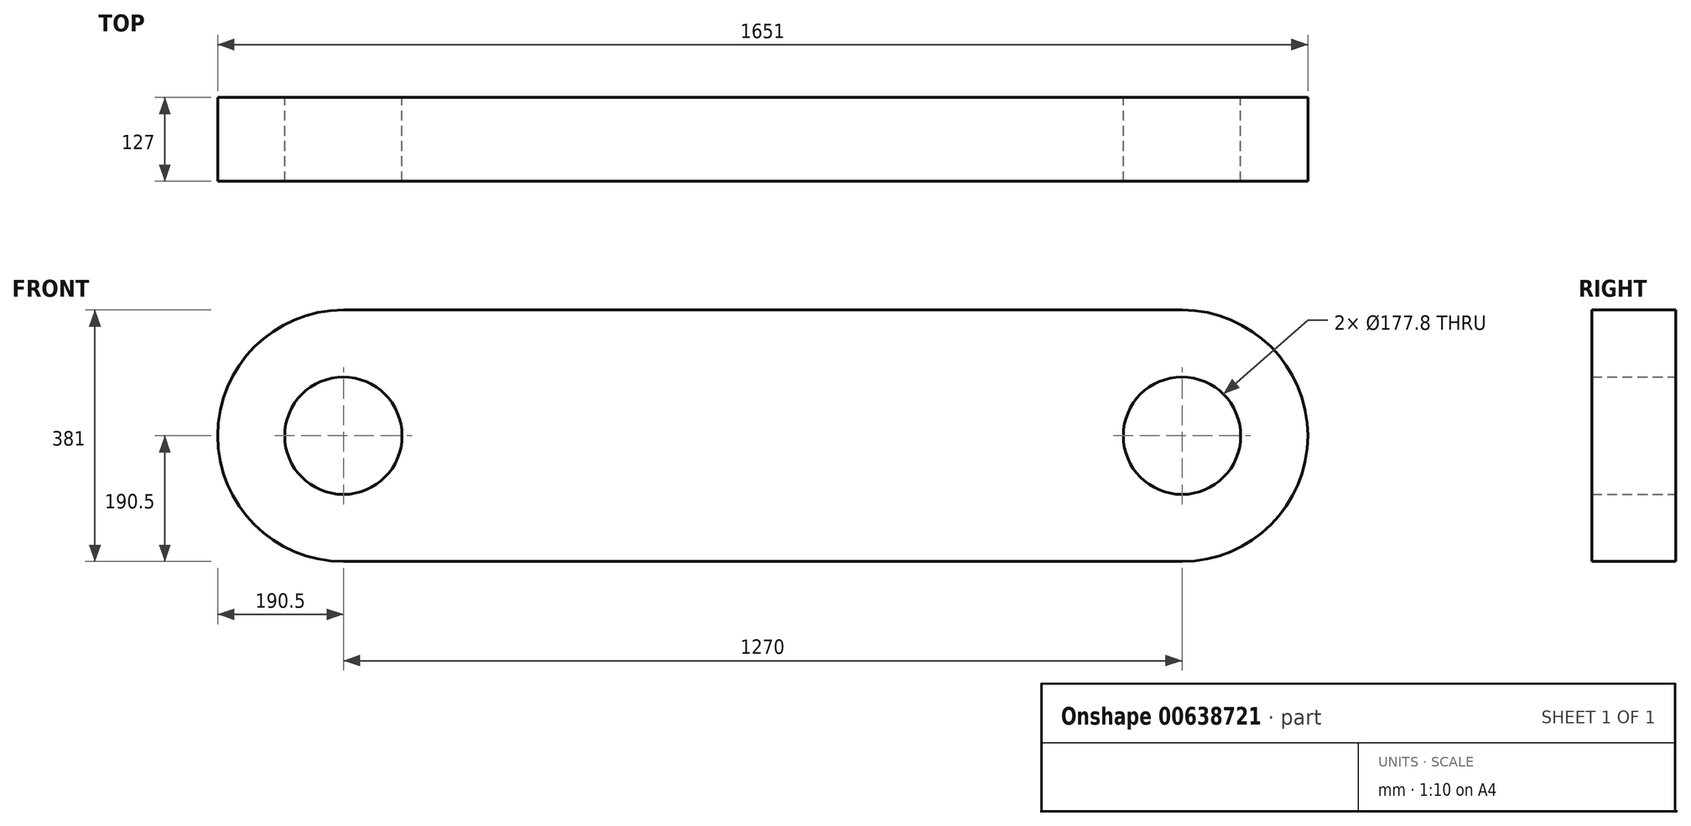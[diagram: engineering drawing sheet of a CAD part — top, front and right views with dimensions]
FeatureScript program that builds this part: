
annotation { "Feature Type Name" : "Feature", "Feature Type Description" : "" }
export const myFeature = defineFeature(function(context is Context, id is Id, definition is map)
    precondition{}
    {
        {
            var Q0;
            Q0=qCreatedBy(makeId("Front.planeOp"),FACE);
            var sketch = newSketch(context, id + "F0", { "sketchPlane" : qUnion([Q0])});
            skArc(sketch, "E0", {"start": v(-635, 190.5) * mm, "mid": v(-825.5, 0) * mm, "end": v(-635, -190.5) * mm});
            skCircle(sketch, "E1", {"center": v(-635, 0) * mm, "radius": 88.9 * mm});
            skLineSegment(sketch, "E2", {"start": v(-635, 190.5) * mm, "end": v(0, 190.5) * mm});
            skLineSegment(sketch, "E3", {"start": v(-635, -190.5) * mm, "end": v(0, -190.5) * mm});
            skArc(sketch, "E4.MirrorCS", {"start": v(635, 190.5) * mm, "mid": v(825.5, 0) * mm, "end": v(635, -190.5) * mm});
            skLineSegment(sketch, "E5.MirrorCS", {"start": v(635, 190.5) * mm, "end": v(0, 190.5) * mm});
            skLineSegment(sketch, "E6.MirrorCS", {"start": v(635, -190.5) * mm, "end": v(0, -190.5) * mm});
            skCircle(sketch, "E7.MirrorC", {"center": v(635, 0) * mm, "radius": 88.9 * mm});
            skSolve(sketch);
        }
        {
            var Q0;
            Q0=makeQuery(id+"F0.imprint","IMPRINT",FACE,{"disambiguationData":[TD([[makeQuery(id+"F0.imprint","IMPRINT",EDGE,{"derivedFrom":sQuery(id+"F0.wireOp",EDGE,"E0")}),1.0]])]});
            extrude(context, id + "F1", {"entities" : qUnion([Q0]), "depth" : 127 * mm, "offsetDistance" : 25.4 * mm});
        }
    });
